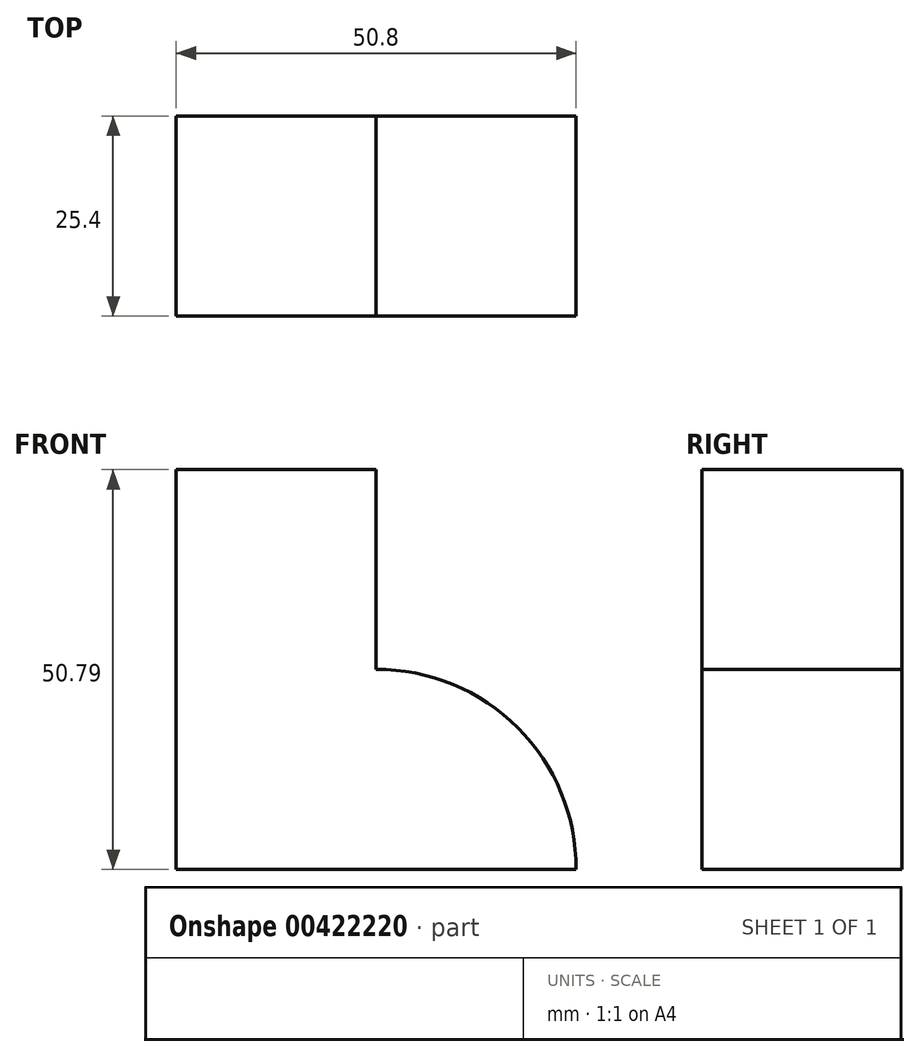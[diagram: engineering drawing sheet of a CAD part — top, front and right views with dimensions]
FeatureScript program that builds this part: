
annotation { "Feature Type Name" : "Feature", "Feature Type Description" : "" }
export const myFeature = defineFeature(function(context is Context, id is Id, definition is map)
    precondition{}
    {
        {
            var Q0;
            Q0=qCreatedBy(makeId("Front.planeOp"),FACE);
            var sketch = newSketch(context, id + "F0", { "sketchPlane" : qUnion([Q0])});
            skLineSegment(sketch, "E0", {"start": v(0, 0) * mm, "end": v(-50.8, 0) * mm});
            skLineSegment(sketch, "E1", {"start": v(-50.8, 0) * mm, "end": v(-50.8, 50.8) * mm});
            skLineSegment(sketch, "E2", {"start": v(-25.4, 50.8) * mm, "end": v(-50.8, 50.8) * mm});
            skLineSegment(sketch, "E3", {"start": v(-25.4, 50.8) * mm, "end": v(-25.4, 25.4) * mm});
            skArc(sketch, "E4", {"start": v(0, 0) * mm, "mid": v(-7.4, 18) * mm, "end": v(-25.4, 25.4) * mm});
            skSolve(sketch);
        }
        {
            var Q0;
            Q0 = qSketchRegion(id + "F0", true);
            extrude(context, id + "F1", {"entities" : qUnion([Q0]), "depth" : 25.4 * mm});
        }
    });
